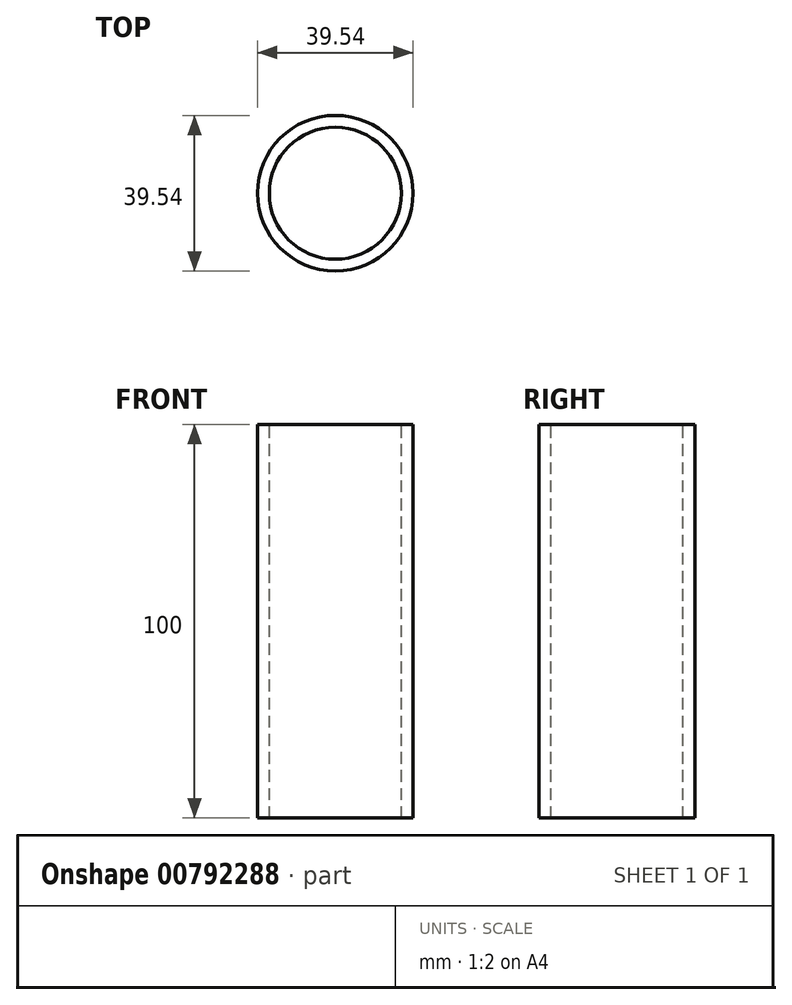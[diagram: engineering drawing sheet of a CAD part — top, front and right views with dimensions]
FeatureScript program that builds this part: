
annotation { "Feature Type Name" : "Feature", "Feature Type Description" : "" }
export const myFeature = defineFeature(function(context is Context, id is Id, definition is map)
    precondition{}
    {
        {
            var Q0;
            Q0=qCreatedBy(makeId("Top.planeOp"),FACE);
            var sketch = newSketch(context, id + "F0", { "sketchPlane" : qUnion([Q0])});
            skCircle(sketch, "E0", {"center": v(0, 0) * mm, "radius": 19.77 * mm});
            skCircle(sketch, "E1.0", {"center": v(0, 0) * mm, "radius": 16.77 * mm});
            skSolve(sketch);
        }
        {
            var Q0;
            Q0=sQuery(id+"F0.wireOp",EDGE,"E1.0");
            var Q1;
            Q1=sQuery(id+"F0.wireOp",EDGE,"E0");
            extrude(context, id + "F1", {"bodyType" : ToolBodyType.SURFACE, "surfaceEntities" : qUnion([Q0, Q1]), "depth" : 100 * mm, "offsetDistance" : 25 * mm});
        }
    });
